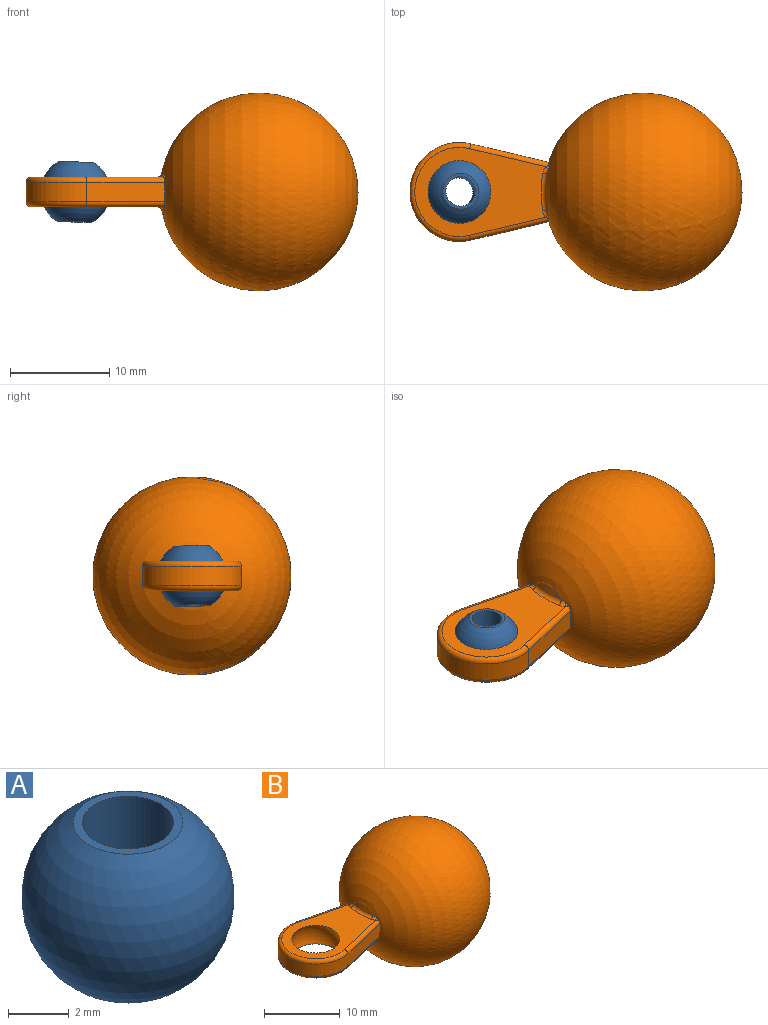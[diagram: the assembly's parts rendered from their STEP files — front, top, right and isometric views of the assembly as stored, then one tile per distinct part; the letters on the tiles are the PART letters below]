
ASSEMBLY  parts=2 mates=1
PART A: 4 faces, bbox 7x7x6 mm
  f0: sphere r=3.5mm, area 131.9mm2, adj f1,f3
  f1: plane 3.61x3.61mm, normal (0,0,1), area 3.1mm2, adj f0,f2
  f2: cylinder r=1.5mm len=6mm, axis (0,0,1), area 56.5mm2, adj f1,f3
  f3: plane 3.61x3.61mm, normal (0,0,-1), area 3.1mm2, adj f0,f2
PART B: 35 faces, bbox 34x20.1x20.1 mm
  f0: plane 1.57x0.47mm, normal (1,0,0), area 0.1mm2, adj f4,f10,f18,f28
  f1: plane 1.57x0.47mm, normal (1,0,0), area 0.1mm2, adj f4,f10,f21,f33
  f2: plane 1.57x0.47mm, normal (1,0,0), area 0.1mm2, adj f6,f10,f16,f24
  f3: cylinder r=5mm len=10mm, axis (0,0,-1), area 36.1mm2, adj f4,f6,f17,f20
  f4: plane 7.84x2mm, normal (0.23,-0.97,0), area 16.1mm2, adj f0,f1,f3,f18,f21
  f5: plane 1.57x0.47mm, normal (1,0,0), area 0.1mm2, adj f6,f10,f19,f29
  f6: plane 7.84x2mm, normal (0.23,0.97,0), area 16.1mm2, adj f2,f3,f5,f16,f19
  f7: plane 13.21x9mm, normal (0,0,1), area 60.9mm2, adj f15,f19,f20,f21,f30,f31,f32
  f8: plane 13.21x9mm, normal (0,0,-1), area 60.9mm2, adj f15,f16,f17,f18,f25,f26,f27
  f9: sphere r=10mm, area 1256.6mm2, adj f23,f26
  f10: cylinder r=3mm len=12.5mm, axis (-1,0,0), area 231mm2, adj f0,f1,f2,f5,f22,f23,f24,f28
  f11: sphere r=10mm, area 1256.6mm2, adj f22,f31
  f12: cylinder r=1.38mm len=13mm, axis (-1,0,0), area 113.1mm2, adj f13,f14
  f13: plane 5x5mm, normal (1,0,0), area 13.6mm2, adj f12,f34
  f14: plane 2.77x2.77mm, normal (1,0,0), area 6mm2, adj f12
  f15: sphere r=3.51mm, area 66.1mm2, adj f7,f8
  f16: cylinder r=0.5mm len=8.03mm, axis (-0.97,0.23,0), area 6.3mm2, adj f2,f6,f8,f17,f24
  f17: torus R=4.5mm, axis (0,0,1), area 13.7mm2, adj f3,f8,f16,f18
  f18: cylinder r=0.5mm len=8.03mm, axis (0.97,0.23,0), area 6.3mm2, adj f0,f4,f8,f17,f28
  f19: cylinder r=0.5mm len=8.03mm, axis (0.97,-0.23,0), area 6.3mm2, adj f5,f6,f7,f20,f29
  f20: torus R=4.5mm, axis (0,0,1), area 13.7mm2, adj f3,f7,f19,f21
  f21: cylinder r=0.5mm len=8.03mm, axis (-0.97,-0.23,0), area 6.3mm2, adj f1,f4,f7,f20,f33
  f22: torus R=2.5mm, axis (1,0,0), area 3.4mm2, adj f10,f11,f29,f30,f32,f33
  f23: torus R=2.5mm, axis (1,0,0), area 3.4mm2, adj f9,f10,f24,f25,f27,f28
  f24: bspline ~0.8x0.55mm, area 0.2mm2, adj f2,f10,f16,f23,f25
  f25: bspline ~1.31x0.74mm, area 0.4mm2, adj f8,f23,f24,f26
  f26: torus R=10.31mm, axis (0,0,1), area 2.6mm2, adj f8,f9,f25,f27
  f27: bspline ~1.31x0.74mm, area 0.4mm2, adj f8,f23,f26,f28
  f28: bspline ~0.8x0.55mm, area 0.2mm2, adj f0,f10,f18,f23,f27
  f29: bspline ~0.8x0.55mm, area 0.2mm2, adj f5,f10,f19,f22,f30
  f30: bspline ~1.31x0.74mm, area 0.4mm2, adj f7,f22,f29,f31
  f31: torus R=10.31mm, axis (0,0,1), area 2.6mm2, adj f7,f11,f30,f32
  f32: bspline ~1.31x0.74mm, area 0.4mm2, adj f7,f22,f31,f33
  f33: bspline ~0.8x0.55mm, area 0.2mm2, adj f1,f10,f21,f22,f32
  f34: torus R=2.5mm, axis (1,0,0), area 13.9mm2, adj f10,f13
PLACE A rot(axis=(-0.43,0.75,-0.5),3.4deg) t=(-0.21,-0.04,-0.17)mm
PLACE B t=(-0.21,-0.04,-0.17)mm fixed
MATE ball A.f2 <-> B.f3  axis (0.04,0.02,1) through (-0.21,-0.04,-0.17)mm
